# Revit family: PA651 Olea circular
name_source: partatom
category: Mobiliario
units: mm (PartAtom-declared; Revit-internal decimal feet)

## family parameters
Compartido = No
Corte con vacíos al cargar = No
Número OmniClass = 23.40.20.00
Punto de cálculo de habitación = No
Se basa en plano de trabajo = No
Siempre vertical = Sí
Título OmniClass = General Furniture and Specialties

## types (1)
- PA651 Papelera Olea
    Acabado Papelera = Corten
    Accessibilidad = Sí
    Altura = 806 mm  [stored 2.64436 ft]
    Comentarios de tipo = Papelera de chapa de acero corten. Concebida para permanecer en el timep sin ningún tipo de mantenimiento. Aro interior para sujeción de la bolsa. Evita procesos contaminantes y contribuye a la sostenibilidad del medio ambiente.
    Diámetro = 4150 mm
    Fabricante = BENITO
    Ficha tecnica = http://www.benito.com
    Instalación = Anclaje recomenadado, mediante 4 tornillos de expansión. No suministrados
    Material Papelera = Acero corten
    Modelo = Papelera Olea
    Referencia = PA651
    URL = https://www.benito.com
    URL Producto = http://www.benito.com

note: [stored X ft] marks values corroborated as IEEE doubles in the binary element streams (Revit-internal decimal feet)

## geometry (parser evidence)
native form markers: Blend x4
no freeform markers — native parametric forms only
